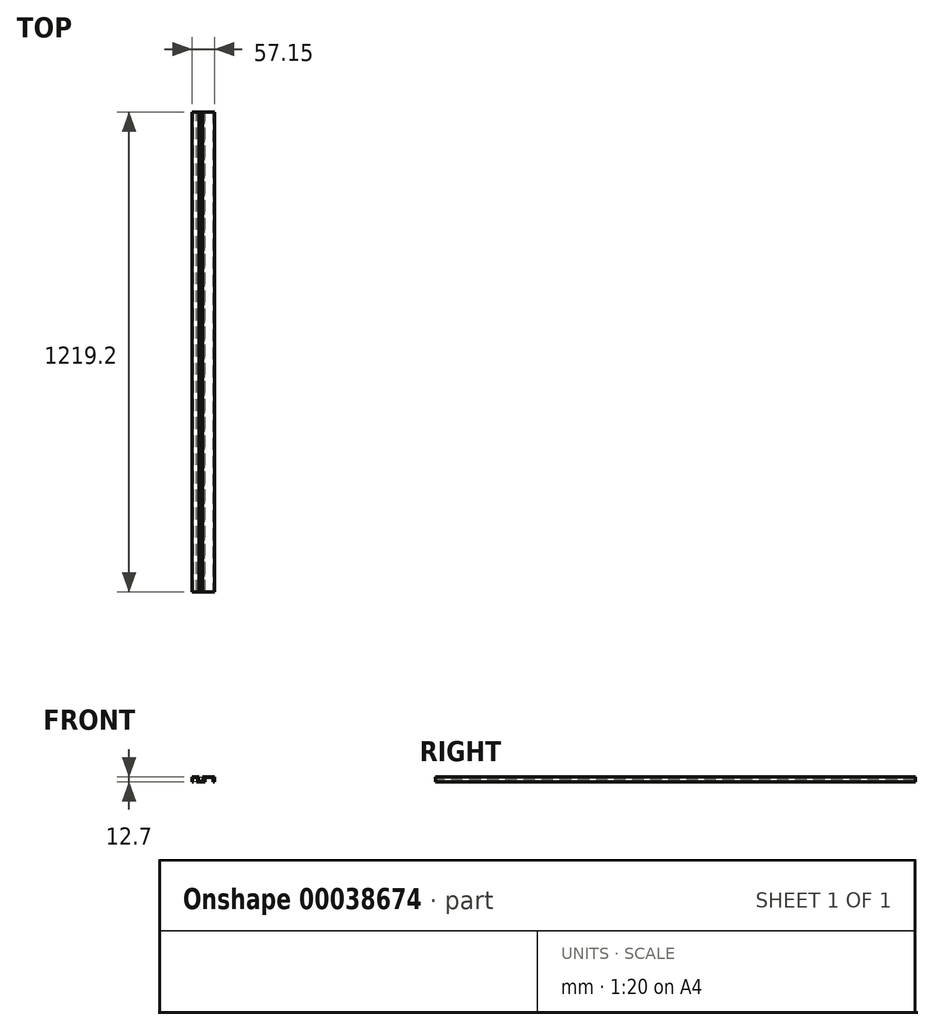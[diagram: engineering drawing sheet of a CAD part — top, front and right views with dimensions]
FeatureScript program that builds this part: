
annotation { "Feature Type Name" : "Feature", "Feature Type Description" : "" }
export const myFeature = defineFeature(function(context is Context, id is Id, definition is map)
    precondition{}
    {
        {
            var Q0;
            Q0=qCreatedBy(makeId("Front.planeOp"),FACE);
            var sketch = newSketch(context, id + "F0", { "sketchPlane" : qUnion([Q0])});
            skLineSegment(sketch, "E0", {"start": v(0, 0) * mm, "end": v(14.29, 0) * mm});
            skLineSegment(sketch, "E1", {"start": v(14.29, 0) * mm, "end": v(14.29, 1.59) * mm});
            skLineSegment(sketch, "E2", {"start": v(14.29, 1.59) * mm, "end": v(7.94, 1.59) * mm});
            skLineSegment(sketch, "E3", {"start": v(7.94, 1.59) * mm, "end": v(7.94, 11.11) * mm});
            skLineSegment(sketch, "E4", {"start": v(7.94, 11.11) * mm, "end": v(14.29, 11.11) * mm});
            skLineSegment(sketch, "E5", {"start": v(14.29, 11.11) * mm, "end": v(14.29, 12.7) * mm});
            skLineSegment(sketch, "E6", {"start": v(14.29, 12.7) * mm, "end": v(0, 12.7) * mm});
            skLineSegment(sketch, "E7", {"start": v(0, 12.7) * mm, "end": v(0, 11.11) * mm});
            skLineSegment(sketch, "E8", {"start": v(0, 11.11) * mm, "end": v(6.35, 11.11) * mm});
            skLineSegment(sketch, "E9", {"start": v(6.35, 11.11) * mm, "end": v(6.35, 1.59) * mm});
            skLineSegment(sketch, "E10", {"start": v(6.35, 1.59) * mm, "end": v(0, 1.59) * mm});
            skLineSegment(sketch, "E11", {"start": v(0, 1.59) * mm, "end": v(0, 0) * mm});
            skLineSegment(sketch, "E12", {"start": v(6.35, 6.35) * mm, "end": v(7.94, 6.35) * mm, "construction": true});
            skLineSegment(sketch, "E13", {"start": v(7.14, 6.35) * mm, "end": v(7.14, 0) * mm, "construction": true});
            skLineSegment(sketch, "E14", {"start": v(7.14, 6.35) * mm, "end": v(7.14, 12.7) * mm, "construction": true});
            skLineSegment(sketch, "E15", {"start": v(10.32, 1.59) * mm, "end": v(10.32, 0) * mm});
            skLineSegment(sketch, "E16", {"start": v(3.97, 11.11) * mm, "end": v(3.97, 12.7) * mm});
            skSolve(sketch);
        }
        {
            var Q0;
            {var subQ3=sQuery(id+"F0.wireOp",EDGE,"E3");Q0=makeQuery(id+"F0.imprint","IMPRINT",FACE,{"disambiguationData":[TD([[makeQuery(id+"F0.imprint","IMPRINT",EDGE,{"derivedFrom":subQ3}),1.0]])]});}
            var Q1;
            Q1=sQuery(id+"F0.wireOp",EDGE,"E14");
            var Q2;
            Q2=sQuery(id+"F0.wireOp",EDGE,"E13");
            var Q3;
            Q3=sQuery(id+"F0.wireOp",EDGE,"E12");
            extrude(context, id + "F1", {"entities" : qUnion([Q0]), "surfaceEntities" : qUnion([Q1, Q2, Q3]), "depth" : 1219.2 * mm});
        }
        {
            var Q0;
            Q0=makeQuery(id+"F1.opExtrude","SWEPT_EDGE",EDGE,{"disambiguationData":[OSD([sQuery(id+"F0.wireOp",EDGE,"E9"),sQuery(id+"F0.wireOp",EDGE,"E10")])]});
            var Q1;
            Q1=makeQuery(id+"F1.opExtrude","SWEPT_EDGE",EDGE,{"disambiguationData":[OSD([sQuery(id+"F0.wireOp",EDGE,"E3"),sQuery(id+"F0.wireOp",EDGE,"E4")])]});
            chamfer(context, id + "F2", {"entities" : qUnion([Q0, Q1]), "width" : 1.59 * mm, "tangentPropagation" : true});
        }
        {
            var Q0;
            Q0=makeQuery(id+"F1.opExtrude","SWEPT_BODY",BODY,{"disambiguationData":[OSD([sQuery(id+"F0.wireOp",EDGE,"E0"),sQuery(id+"F0.wireOp",EDGE,"E2"),sQuery(id+"F0.wireOp",EDGE,"E3"),sQuery(id+"F0.wireOp",EDGE,"E4"),sQuery(id+"F0.wireOp",EDGE,"E5"),sQuery(id+"F0.wireOp",EDGE,"E6"),sQuery(id+"F0.wireOp",EDGE,"E8"),sQuery(id+"F0.wireOp",EDGE,"E9"),sQuery(id+"F0.wireOp",EDGE,"E10"),sQuery(id+"F0.wireOp",EDGE,"E11"),sQuery(id+"F0.wireOp",EDGE,"E15"),sQuery(id+"F0.wireOp",EDGE,"E16")])]});
            var Q1;
            Q1=makeQuery(id+"F1.opExtrude","SWEPT_FACE",FACE,{"disambiguationData":[OSD([sQuery(id+"F0.wireOp",EDGE,"E5")])]});
            mirror(context, id + "F3", {"operationType" : NewBodyOperationType.ADD, "entities" : qUnion([Q0]), "mirrorPlane" : qUnion([Q1])});
        }
        {
            var Q0;
            Q0=makeQuery(id+"F1.opExtrude","SWEPT_BODY",BODY,{"disambiguationData":[OSD([sQuery(id+"F0.wireOp",EDGE,"E0"),sQuery(id+"F0.wireOp",EDGE,"E2"),sQuery(id+"F0.wireOp",EDGE,"E3"),sQuery(id+"F0.wireOp",EDGE,"E4"),sQuery(id+"F0.wireOp",EDGE,"E5"),sQuery(id+"F0.wireOp",EDGE,"E6"),sQuery(id+"F0.wireOp",EDGE,"E8"),sQuery(id+"F0.wireOp",EDGE,"E9"),sQuery(id+"F0.wireOp",EDGE,"E10"),sQuery(id+"F0.wireOp",EDGE,"E11"),sQuery(id+"F0.wireOp",EDGE,"E15"),sQuery(id+"F0.wireOp",EDGE,"E16")])]});
            var Q1;
            Q1=makeQuery(id+"F3.opPattern","COPY",FACE,{"derivedFrom":makeQuery(id+"F1.opExtrude","SWEPT_FACE",FACE,{"disambiguationData":[OSD([sQuery(id+"F0.wireOp",EDGE,"E11")])]}),"instanceName":"1"});
            mirror(context, id + "F4", {"operationType" : NewBodyOperationType.ADD, "entities" : qUnion([Q0]), "mirrorPlane" : qUnion([Q1])});
        }
        {
            var Q0;
            {var subQ0=makeQuery(id+"F1.opExtrude","CAP_FACE",FACE,{"disambiguationData":[OSD([sQuery(id+"F0.wireOp",EDGE,"E0"),sQuery(id+"F0.wireOp",EDGE,"E2"),sQuery(id+"F0.wireOp",EDGE,"E3"),sQuery(id+"F0.wireOp",EDGE,"E4"),sQuery(id+"F0.wireOp",EDGE,"E5"),sQuery(id+"F0.wireOp",EDGE,"E6"),sQuery(id+"F0.wireOp",EDGE,"E8"),sQuery(id+"F0.wireOp",EDGE,"E9"),sQuery(id+"F0.wireOp",EDGE,"E10"),sQuery(id+"F0.wireOp",EDGE,"E11"),sQuery(id+"F0.wireOp",EDGE,"E15"),sQuery(id+"F0.wireOp",EDGE,"E16")])],"isStart":false});var subQ1=makeQuery(id+"F3.boolean.opBoolean","MERGE",FACE,{"derivedFrom":[subQ0,makeQuery(id+"F3.opPattern","COPY",FACE,{"derivedFrom":subQ0,"instanceName":"1"})]});Q0=makeQuery(id+"F4.boolean.opBoolean","MERGE",FACE,{"derivedFrom":[subQ1,makeQuery(id+"F4.opPattern","COPY",FACE,{"derivedFrom":subQ1,"instanceName":"1"})]});}
            var sketch = newSketch(context, id + "F5", { "sketchPlane" : qUnion([Q0])});
            skLineSegment(sketch, "E17", {"start": v(22.23, 12.7) * mm, "end": v(57.15, 12.7) * mm});
            skLineSegment(sketch, "E18", {"start": v(57.15, 12.7) * mm, "end": v(57.15, 0) * mm});
            skLineSegment(sketch, "E19", {"start": v(57.15, 0) * mm, "end": v(22.23, 0) * mm});
            skLineSegment(sketch, "E20", {"start": v(22.23, 12.7) * mm, "end": v(22.23, 0) * mm});
            skSolve(sketch);
        }
        {
            var Q0;
            Q0=qSketchRegion(id+"F5",true);
            extrude(context, id + "F6", {"entities" : qUnion([Q0]), "operationType" : NewBodyOperationType.REMOVE, "endBound" : BoundingType.THROUGH_ALL, "oppositeDirection" : true, "depth" : 25.4 * mm});
        }
        {
            var Q0;
            Q0=makeQuery(id+"F1.opExtrude","SWEPT_BODY",BODY,{"disambiguationData":[OSD([sQuery(id+"F0.wireOp",EDGE,"E0"),sQuery(id+"F0.wireOp",EDGE,"E2"),sQuery(id+"F0.wireOp",EDGE,"E3"),sQuery(id+"F0.wireOp",EDGE,"E4"),sQuery(id+"F0.wireOp",EDGE,"E5"),sQuery(id+"F0.wireOp",EDGE,"E6"),sQuery(id+"F0.wireOp",EDGE,"E8"),sQuery(id+"F0.wireOp",EDGE,"E9"),sQuery(id+"F0.wireOp",EDGE,"E10"),sQuery(id+"F0.wireOp",EDGE,"E11"),sQuery(id+"F0.wireOp",EDGE,"E15"),sQuery(id+"F0.wireOp",EDGE,"E16")])]});
            var Q1;
            Q1=makeQuery(id+"F1.opExtrude","SWEPT_FACE",FACE,{"disambiguationData":[OSD([sQuery(id+"F0.wireOp",EDGE,"E11")])]});
            mirror(context, id + "F7", {"operationType" : NewBodyOperationType.ADD, "entities" : qUnion([Q0]), "mirrorPlane" : qUnion([Q1])});
        }
        {
            var Q0;
            {var subQ0=makeQuery(id+"F1.opExtrude","CAP_FACE",FACE,{"disambiguationData":[OSD([sQuery(id+"F0.wireOp",EDGE,"E0"),sQuery(id+"F0.wireOp",EDGE,"E2"),sQuery(id+"F0.wireOp",EDGE,"E3"),sQuery(id+"F0.wireOp",EDGE,"E4"),sQuery(id+"F0.wireOp",EDGE,"E5"),sQuery(id+"F0.wireOp",EDGE,"E6"),sQuery(id+"F0.wireOp",EDGE,"E8"),sQuery(id+"F0.wireOp",EDGE,"E9"),sQuery(id+"F0.wireOp",EDGE,"E10"),sQuery(id+"F0.wireOp",EDGE,"E11"),sQuery(id+"F0.wireOp",EDGE,"E15"),sQuery(id+"F0.wireOp",EDGE,"E16")])],"isStart":false});var subQ1=makeQuery(id+"F3.boolean.opBoolean","MERGE",FACE,{"derivedFrom":[subQ0,makeQuery(id+"F3.opPattern","COPY",FACE,{"derivedFrom":subQ0,"instanceName":"1"})]});var subQ2=makeQuery(id+"F4.boolean.opBoolean","MERGE",FACE,{"derivedFrom":[subQ1,makeQuery(id+"F4.opPattern","COPY",FACE,{"derivedFrom":subQ1,"instanceName":"1"})]});Q0=makeQuery(id+"F7.boolean.opBoolean","MERGE",FACE,{"derivedFrom":[subQ2,makeQuery(id+"F7.opPattern","COPY",FACE,{"derivedFrom":subQ2,"instanceName":"1"})]});}
            var sketch = newSketch(context, id + "F8", { "sketchPlane" : qUnion([Q0])});
            skLineSegment(sketch, "E21", {"start": v(7.94, 9.53) * mm, "end": v(7.94, 12.7) * mm});
            skSolve(sketch);
        }
        {
            var Q0;
            Q0 = qSketchRegion(id + "F8", true);
            var Q1;
            {var subQ5=sQuery(id+"F8.wireOp",EDGE,"E21");Q1=makeQuery(id+"F8.imprint","IMPRINT",FACE,{"disambiguationData":[TD([[makeQuery(id+"F8.imprint","IMPRINT",EDGE,{"derivedFrom":subQ5}),-1.0]])]});}
            extrude(context, id + "F9", {"entities" : qUnion([Q0, Q1]), "operationType" : NewBodyOperationType.REMOVE, "endBound" : BoundingType.THROUGH_ALL, "oppositeDirection" : true, "depth" : 25.4 * mm});
        }
        {
            var Q0;
            {var subQ0=makeQuery(id+"F1.opExtrude","CAP_FACE",FACE,{"disambiguationData":[OSD([sQuery(id+"F0.wireOp",EDGE,"E0"),sQuery(id+"F0.wireOp",EDGE,"E2"),sQuery(id+"F0.wireOp",EDGE,"E3"),sQuery(id+"F0.wireOp",EDGE,"E4"),sQuery(id+"F0.wireOp",EDGE,"E5"),sQuery(id+"F0.wireOp",EDGE,"E6"),sQuery(id+"F0.wireOp",EDGE,"E8"),sQuery(id+"F0.wireOp",EDGE,"E9"),sQuery(id+"F0.wireOp",EDGE,"E10"),sQuery(id+"F0.wireOp",EDGE,"E11"),sQuery(id+"F0.wireOp",EDGE,"E15"),sQuery(id+"F0.wireOp",EDGE,"E16")])],"isStart":false});var subQ1=makeQuery(id+"F3.boolean.opBoolean","MERGE",FACE,{"derivedFrom":[subQ0,makeQuery(id+"F3.opPattern","COPY",FACE,{"derivedFrom":subQ0,"instanceName":"1"})]});var subQ2=makeQuery(id+"F4.boolean.opBoolean","MERGE",FACE,{"derivedFrom":[subQ1,makeQuery(id+"F4.opPattern","COPY",FACE,{"derivedFrom":subQ1,"instanceName":"1"})]});Q0=makeQuery(id+"F7.boolean.opBoolean","MERGE",FACE,{"derivedFrom":[subQ2,makeQuery(id+"F7.opPattern","COPY",FACE,{"derivedFrom":subQ2,"instanceName":"1"})]});}
            var sketch = newSketch(context, id + "F10", { "sketchPlane" : qUnion([Q0])});
            skLineSegment(sketch, "E22", {"start": v(7.94, 12.7) * mm, "end": v(34.93, 12.7) * mm});
            skLineSegment(sketch, "E23", {"start": v(34.93, 12.7) * mm, "end": v(34.93, 0) * mm});
            skLineSegment(sketch, "E24", {"start": v(34.93, 0) * mm, "end": v(30.96, 0) * mm});
            skLineSegment(sketch, "E25", {"start": v(30.96, 0) * mm, "end": v(30.96, 7.94) * mm});
            skLineSegment(sketch, "E26", {"start": v(30.96, 7.94) * mm, "end": v(33.34, 7.94) * mm});
            skLineSegment(sketch, "E27", {"start": v(33.34, 7.94) * mm, "end": v(33.34, 11.11) * mm});
            skLineSegment(sketch, "E28", {"start": v(33.34, 11.11) * mm, "end": v(7.94, 11.11) * mm});
            skLineSegment(sketch, "E29", {"start": v(7.94, 11.11) * mm, "end": v(7.94, 7.94) * mm});
            skLineSegment(sketch, "E30", {"start": v(7.94, 7.94) * mm, "end": v(10.32, 7.94) * mm});
            skLineSegment(sketch, "E31", {"start": v(10.32, 7.94) * mm, "end": v(10.32, 1.59) * mm});
            skSolve(sketch);
        }
        {
            var Q0;
            {var subQ3=sQuery(id+"F10.wireOp",EDGE,"E22");Q0=makeQuery(id+"F10.imprint","IMPRINT",FACE,{"disambiguationData":[TD([[makeQuery(id+"F10.imprint","IMPRINT",EDGE,{"derivedFrom":subQ3}),-1.0]])]});}
            var Q1;
            {var subQ1=sQuery(id+"F10.wireOp",EDGE,"E30");Q1=makeQuery(id+"F10.imprint","IMPRINT",FACE,{"disambiguationData":[TD([[makeQuery(id+"F10.imprint","IMPRINT",EDGE,{"derivedFrom":subQ1}),-1.0]])]});}
            var Q2;
            {var subQ0=makeQuery(id+"F1.opExtrude","CAP_FACE",FACE,{"disambiguationData":[OSD([sQuery(id+"F0.wireOp",EDGE,"E0"),sQuery(id+"F0.wireOp",EDGE,"E2"),sQuery(id+"F0.wireOp",EDGE,"E3"),sQuery(id+"F0.wireOp",EDGE,"E4"),sQuery(id+"F0.wireOp",EDGE,"E5"),sQuery(id+"F0.wireOp",EDGE,"E6"),sQuery(id+"F0.wireOp",EDGE,"E8"),sQuery(id+"F0.wireOp",EDGE,"E9"),sQuery(id+"F0.wireOp",EDGE,"E10"),sQuery(id+"F0.wireOp",EDGE,"E11"),sQuery(id+"F0.wireOp",EDGE,"E15"),sQuery(id+"F0.wireOp",EDGE,"E16")])],"isStart":true});var subQ1=makeQuery(id+"F3.boolean.opBoolean","MERGE",FACE,{"derivedFrom":[subQ0,makeQuery(id+"F3.opPattern","COPY",FACE,{"derivedFrom":subQ0,"instanceName":"1"})]});var subQ2=makeQuery(id+"F4.boolean.opBoolean","MERGE",FACE,{"derivedFrom":[subQ1,makeQuery(id+"F4.opPattern","COPY",FACE,{"derivedFrom":subQ1,"instanceName":"1"})]});Q2=makeQuery(id+"F7.boolean.opBoolean","MERGE",FACE,{"derivedFrom":[subQ2,makeQuery(id+"F7.opPattern","COPY",FACE,{"derivedFrom":subQ2,"instanceName":"1"})]});}
            extrude(context, id + "F11", {"entities" : qUnion([Q0, Q1]), "operationType" : NewBodyOperationType.ADD, "endBound" : BoundingType.UP_TO_SURFACE, "oppositeDirection" : true, "endBoundEntityFace" : qUnion([Q2]), "depth" : 25.4 * mm});
        }
    });
